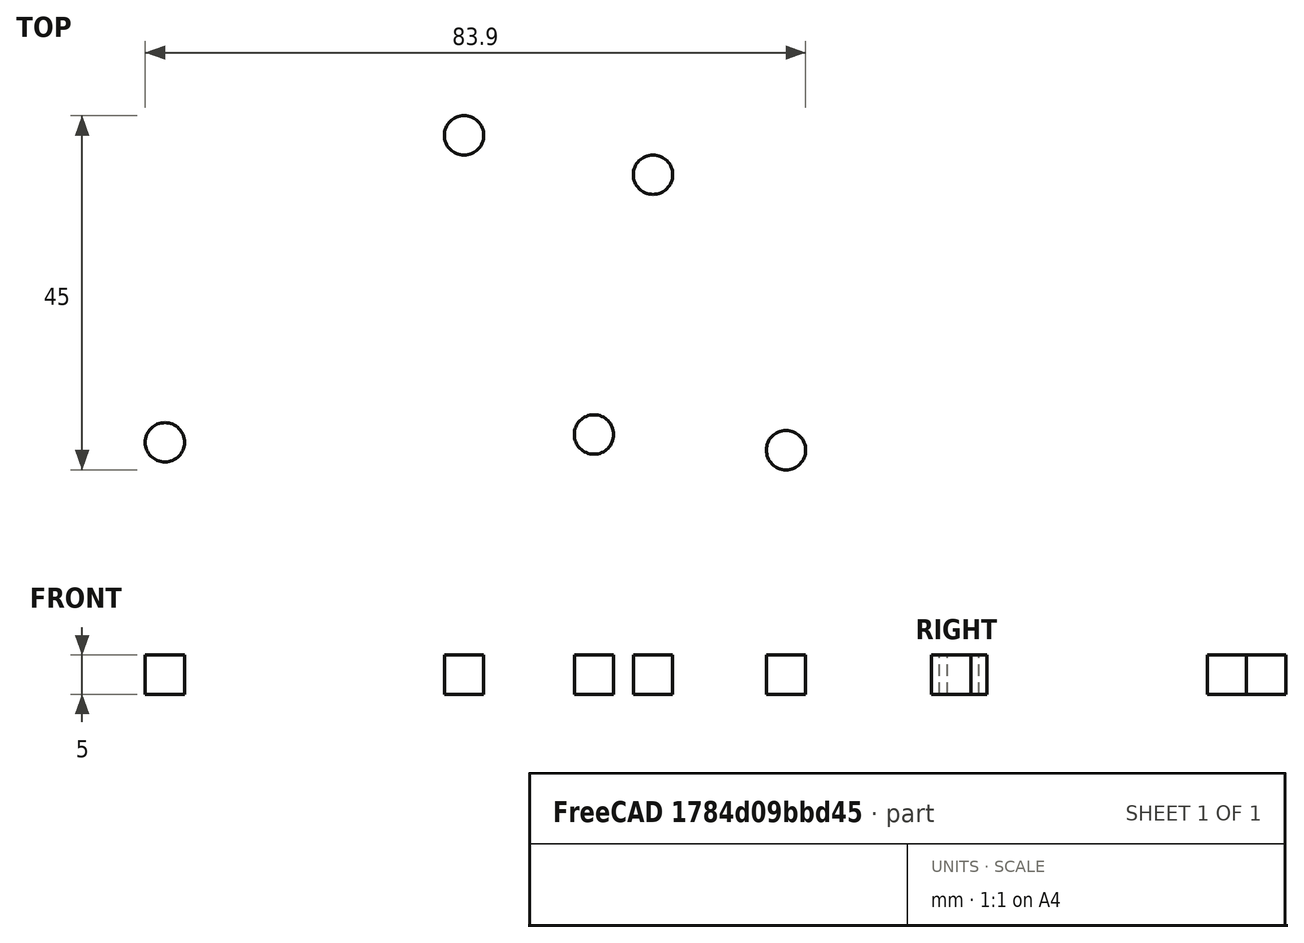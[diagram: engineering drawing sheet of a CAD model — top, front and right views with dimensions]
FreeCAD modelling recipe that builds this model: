
FCSTD DOCUMENT  (FreeCAD 0.18.4R)
Label: acer_motherboard_case
License: All rights reserved
LicenseURL: http://en.wikipedia.org/wiki/All_rights_reserved
objects: Part::RuledSurface×6, Part::Cylinder×5, PartDesign::Body×1
note: 12 computed .brp shape members not serialized (recipe doc carries the construction recipe); baked Part::Feature solids carry a one-line shape summary decoded from their .brp

FEATURE [PartDesign::Body] Body
  Origin = -> Origin
FEATURE [Part::Cylinder] Cylinder  label="screwhole_base_S1"
  Angle = 360
  AttacherType = Attacher::AttachEngine3D
  Height = 5
  Placement = pos=(0,5.5,0) rot=(0,0,1;0rad)
  Radius = 2.5
FEATURE [Part::Cylinder] Cylinder001  label="screwhole_base_S2"
  Angle = 360
  AttacherType = Attacher::AttachEngine3D
  Height = 5
  Placement = pos=(24.4,3.5,0) rot=(0,0,1;0rad)
  Radius = 2.5
FEATURE [Part::Cylinder] Cylinder002  label="screwhole_base_S3"
  Angle = 360
  AttacherType = Attacher::AttachEngine3D
  Height = 5
  Placement = pos=(7.5,38.5,0) rot=(0,0,1;0rad)
  Radius = 2.5
FEATURE [Part::Cylinder] Cylinder003  label="screwhole_base_S4"
  Angle = 360
  AttacherType = Attacher::AttachEngine3D
  Height = 5
  Placement = pos=(-16.5,43.5,0) rot=(0,0,1;0rad)
  Radius = 2.5
FEATURE [Part::Cylinder] Cylinder004  label="screwhole_base_S5"
  Angle = 360
  AttacherType = Attacher::AttachEngine3D
  Height = 5
  Placement = pos=(-54.5,4.5,0) rot=(0,0,1;0rad)
  Radius = 2.5
FEATURE [Part::RuledSurface] Ruled_Surface
  Curve1 = -> Cylinder [Edge1]
  Curve2 = -> Cylinder001 [Edge1]
  Orientation = 0
FEATURE [Part::RuledSurface] Ruled_Surface001
  Curve1 = -> Cylinder002 [Edge1]
  Curve2 = -> Cylinder001 [Edge1]
  Orientation = 0
FEATURE [Part::RuledSurface] Ruled_Surface002
  Curve1 = -> Cylinder [Edge1]
  Curve2 = -> Ruled_Surface001 [Edge1]
  Orientation = 0
FEATURE [Part::RuledSurface] Ruled_Surface003
  Curve1 = -> Cylinder003 [Edge1]
  Curve2 = -> Cylinder002 [Edge1]
  Orientation = 0
FEATURE [Part::RuledSurface] Ruled_Surface004
  Curve1 = -> Ruled_Surface003 [Edge1]
  Curve2 = -> Cylinder004 [Edge1]
  Orientation = 0
FEATURE [Part::RuledSurface] Ruled_Surface005
  Curve1 = -> Ruled_Surface004 [Edge3]
  Curve2 = -> Ruled_Surface [Edge1]
  Orientation = 0
